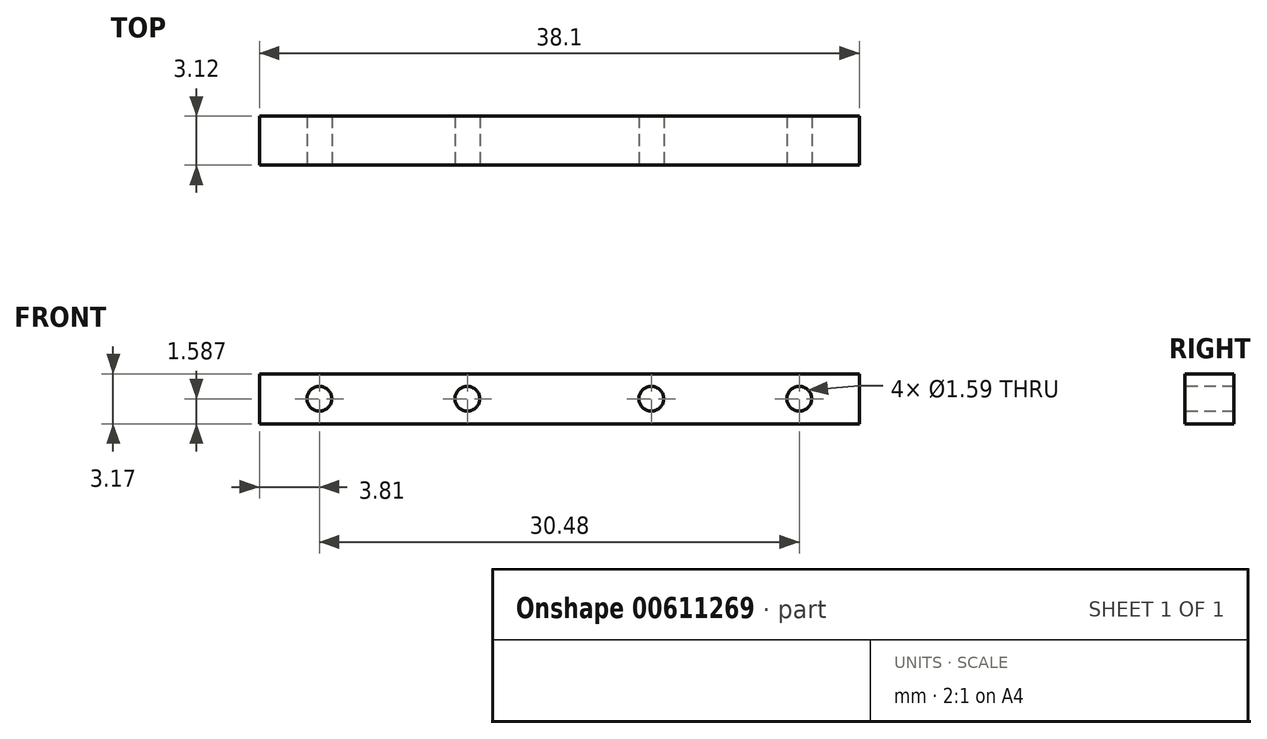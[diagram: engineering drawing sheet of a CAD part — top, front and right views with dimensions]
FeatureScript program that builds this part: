
annotation { "Feature Type Name" : "Feature", "Feature Type Description" : "" }
export const myFeature = defineFeature(function(context is Context, id is Id, definition is map)
    precondition{}
    {
        {
            var Q0;
            Q0=qCreatedBy(makeId("Top.planeOp"),FACE);
            var sketch = newSketch(context, id + "F0", { "sketchPlane" : qUnion([Q0])});
            skLineSegment(sketch, "E0.bottom", {"start": v(-19.05, 0) * mm, "end": v(19.05, 0) * mm});
            skLineSegment(sketch, "E0.top", {"start": v(-19.05, 3.12) * mm, "end": v(19.05, 3.12) * mm});
            skLineSegment(sketch, "E0.left", {"start": v(-19.05, 0) * mm, "end": v(-19.05, 3.12) * mm});
            skLineSegment(sketch, "E0.right", {"start": v(19.05, 0) * mm, "end": v(19.05, 3.12) * mm});
            skSolve(sketch);
        }
        {
            var Q0;
            Q0=makeQuery(id+"F0.imprint","IMPRINT",FACE,{"disambiguationData":[TD([[makeQuery(id+"F0.imprint","IMPRINT",EDGE,{"derivedFrom":sQuery(id+"F0.wireOp",EDGE,"E0.bottom")}),1.0]])]});
            extrude(context, id + "F1", {"entities" : qUnion([Q0]), "depth" : 3.17 * mm, "offsetDistance" : 25.4 * mm});
        }
        {
            var Q0;
            Q0=makeQuery(id+"F1.opExtrude","SWEPT_FACE",FACE,{"disambiguationData":[OSD([sQuery(id+"F0.wireOp",EDGE,"E0.bottom")])]});
            var sketch = newSketch(context, id + "F2", { "sketchPlane" : qUnion([Q0])});
            skCircle(sketch, "E1", {"center": v(-15.24, 1.59) * mm, "radius": 0.8 * mm});
            skPoint(sketch, "E1.centerSnap0", {"position": v(-19.05, 1.59) * mm});
            skCircle(sketch, "E2", {"center": v(-5.84, 1.59) * mm, "radius": 0.8 * mm});
            skCircle(sketch, "E3", {"center": v(5.84, 1.59) * mm, "radius": 0.8 * mm});
            skCircle(sketch, "E4", {"center": v(15.24, 1.59) * mm, "radius": 0.8 * mm});
            skSolve(sketch);
        }
        {
            var Q0;
            Q0=makeQuery(id+"F2.imprint","IMPRINT",FACE,{"disambiguationData":[TD([[makeQuery(id+"F2.imprint","IMPRINT",EDGE,{"derivedFrom":sQuery(id+"F2.wireOp",EDGE,"E1")}),1.0]])]});
            var Q1;
            Q1=makeQuery(id+"F2.imprint","IMPRINT",FACE,{"disambiguationData":[TD([[makeQuery(id+"F2.imprint","IMPRINT",EDGE,{"derivedFrom":sQuery(id+"F2.wireOp",EDGE,"E2")}),1.0]])]});
            var Q2;
            Q2=makeQuery(id+"F2.imprint","IMPRINT",FACE,{"disambiguationData":[TD([[makeQuery(id+"F2.imprint","IMPRINT",EDGE,{"derivedFrom":sQuery(id+"F2.wireOp",EDGE,"E3")}),1.0]])]});
            var Q3;
            Q3=makeQuery(id+"F2.imprint","IMPRINT",FACE,{"disambiguationData":[TD([[makeQuery(id+"F2.imprint","IMPRINT",EDGE,{"derivedFrom":sQuery(id+"F2.wireOp",EDGE,"E4")}),1.0]])]});
            extrude(context, id + "F3", {"entities" : qUnion([Q0, Q1, Q2, Q3]), "operationType" : NewBodyOperationType.REMOVE, "oppositeDirection" : true, "depth" : 25.4 * mm, "offsetDistance" : 25.4 * mm});
        }
    });
